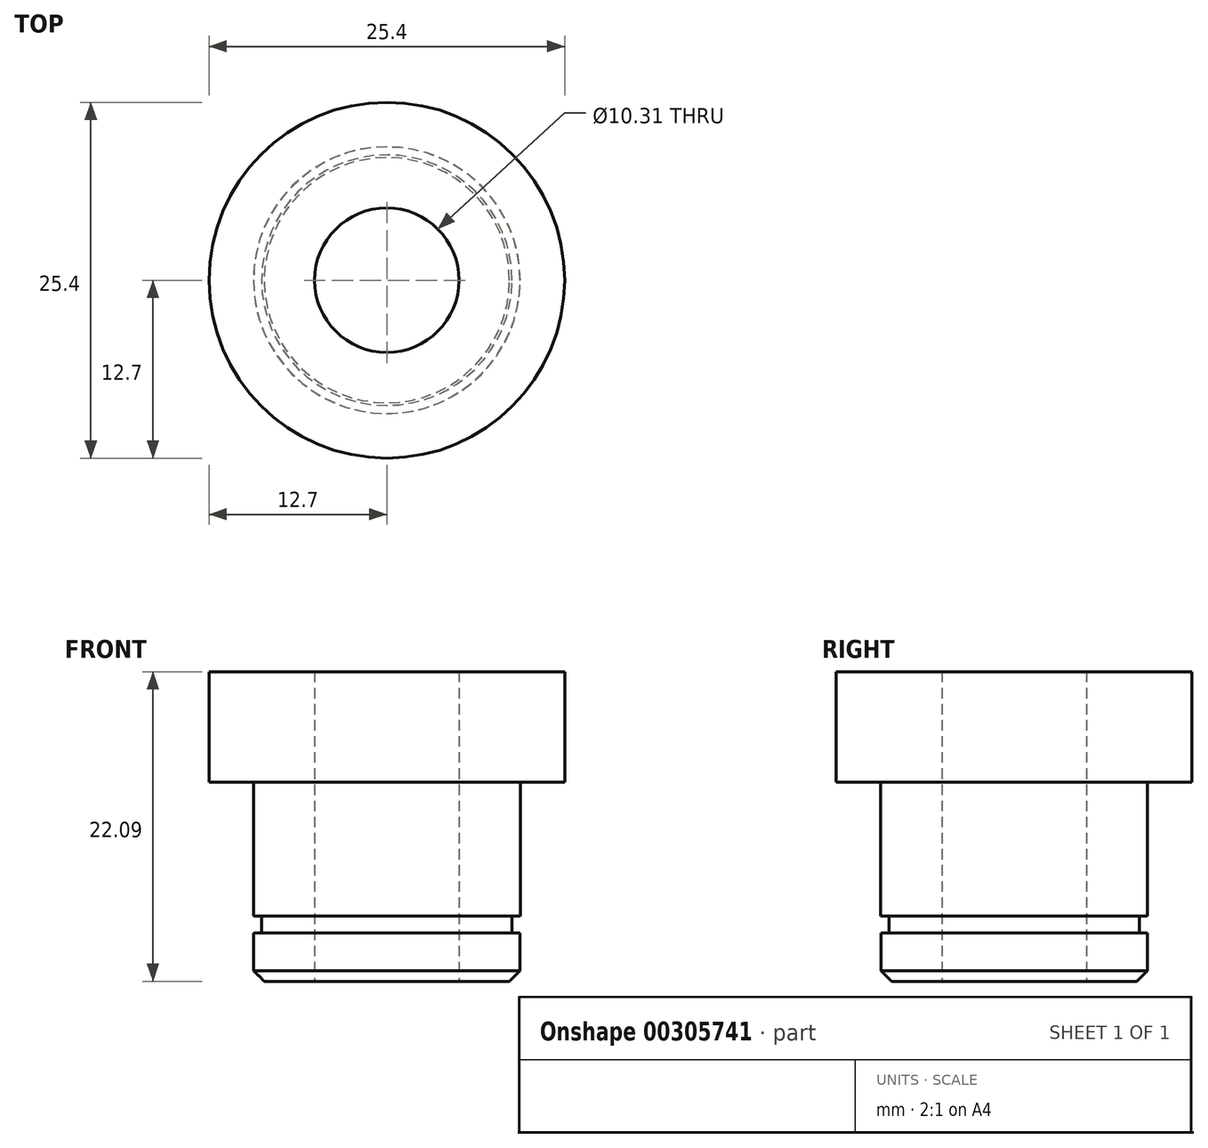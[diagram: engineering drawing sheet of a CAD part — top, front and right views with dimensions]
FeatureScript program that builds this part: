
annotation { "Feature Type Name" : "Feature", "Feature Type Description" : "" }
export const myFeature = defineFeature(function(context is Context, id is Id, definition is map)
    precondition{}
    {
        {
            var Q0;
            Q0=qCreatedBy(makeId("Top.planeOp"),FACE);
            var sketch = newSketch(context, id + "F0", { "sketchPlane" : qUnion([Q0])});
            skCircle(sketch, "E0", {"center": v(0, 0) * mm, "radius": 12.7 * mm});
            skSolve(sketch);
        }
        {
            var Q0;
            Q0 = qSketchRegion(id + "F0", true);
            extrude(context, id + "F1", {"entities" : qUnion([Q0]), "depth" : 7.87 * mm});
        }
        {
            var Q0;
            Q0=qCreatedBy(makeId("Top.planeOp"),FACE);
            var sketch = newSketch(context, id + "F2", { "sketchPlane" : qUnion([Q0])});
            skCircle(sketch, "E1", {"center": v(0, 0) * mm, "radius": 9.53 * mm});
            skSolve(sketch);
        }
        {
            var Q0;
            Q0 = qSketchRegion(id + "F2", true);
            extrude(context, id + "F3", {"entities" : qUnion([Q0]), "operationType" : NewBodyOperationType.ADD, "oppositeDirection" : true, "depth" : 9.58 * mm});
        }
        {
            var Q0;
            Q0=makeQuery(id+"F3.opExtrude","CAP_FACE",FACE,{"disambiguationData":[OSD([sQuery(id+"F2.wireOp",EDGE,"E1")])],"isStart":false});
            var sketch = newSketch(context, id + "F4", { "sketchPlane" : qUnion([Q0])});
            skCircle(sketch, "E2", {"center": v(0, 0) * mm, "radius": 8.94 * mm});
            skSolve(sketch);
        }
        {
            var Q0;
            Q0 = qSketchRegion(id + "F4", true);
            extrude(context, id + "F5", {"entities" : qUnion([Q0]), "operationType" : NewBodyOperationType.ADD, "depth" : 1.2 * mm});
        }
        {
            var Q0;
            Q0=makeQuery(id+"F5.opExtrude","CAP_FACE",FACE,{"disambiguationData":[OSD([sQuery(id+"F4.wireOp",EDGE,"E2")])],"isStart":false});
            var sketch = newSketch(context, id + "F6", { "sketchPlane" : qUnion([Q0])});
            skCircle(sketch, "E3", {"center": v(0, 0) * mm, "radius": 9.51 * mm});
            skSolve(sketch);
        }
        {
            var Q0;
            Q0 = qSketchRegion(id + "F6", true);
            extrude(context, id + "F7", {"entities" : qUnion([Q0]), "operationType" : NewBodyOperationType.ADD, "depth" : 3.45 * mm});
        }
        {
            var Q0;
            Q0=makeQuery(id+"F7.opExtrude","CAP_EDGE",EDGE,{"disambiguationData":[OSD([sQuery(id+"F6.wireOp",EDGE,"E3")])],"isStart":false});
            chamfer(context, id + "F8", {"entities" : qUnion([Q0]), "width" : 0.76 * mm, "tangentPropagation" : true});
        }
        {
            var Q0;
            Q0=makeQuery(id+"F7.opExtrude","CAP_FACE",FACE,{"disambiguationData":[OSD([sQuery(id+"F6.wireOp",EDGE,"E3")])],"isStart":false});
            var sketch = newSketch(context, id + "F9", { "sketchPlane" : qUnion([Q0])});
            skPoint(sketch, "E4", {"position": v(0, 0) * mm});
            skSolve(sketch);
        }
        {
            var Q0;
            Q0=sQuery(id+"F9.wireOp",VERTEX,"E4");
            var Q1;
            Q1=makeQuery(id+"F1.opExtrude","SWEPT_BODY",BODY,{"disambiguationData":[OSD([sQuery(id+"F0.wireOp",EDGE,"E0")])]});
            hole(context, id + "F10", {"style" : HoleStyle.SIMPLE, "endStyle" : HoleEndStyle.THROUGH, "holeDiameter" : 10.3 * mm, "tappedDepth" : 24.13 * mm, "tapClearance" : 3, "startFromSketch" : true, "locations" : qUnion([Q0]), "scope" : qUnion([Q1])});
        }
    });
